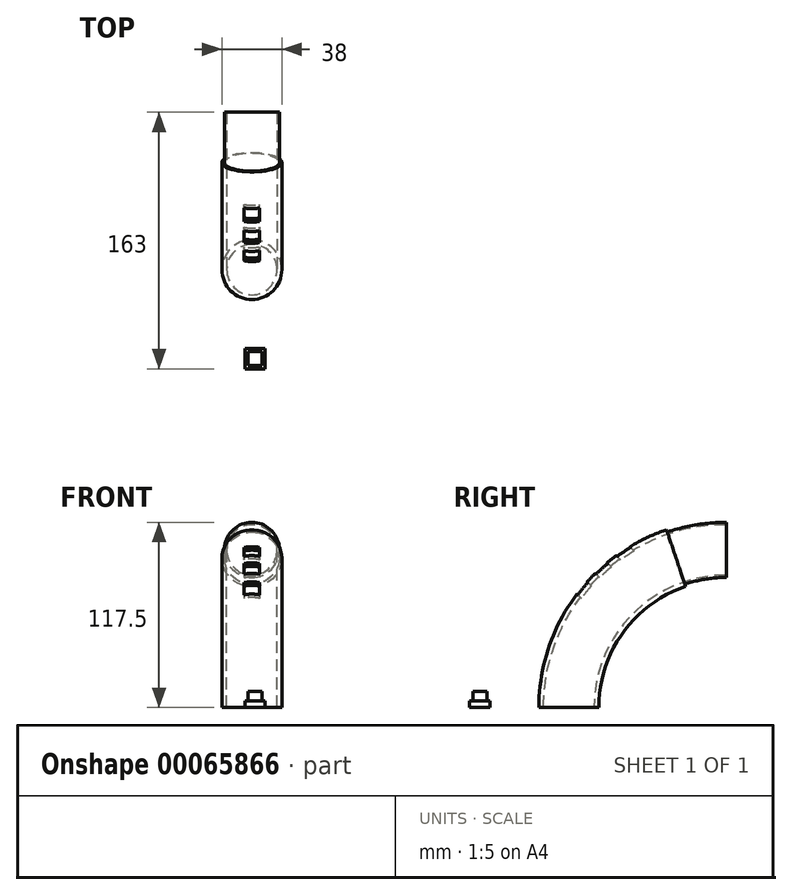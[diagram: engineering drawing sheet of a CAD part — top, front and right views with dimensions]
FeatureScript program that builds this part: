
annotation { "Feature Type Name" : "Feature", "Feature Type Description" : "" }
export const myFeature = defineFeature(function(context is Context, id is Id, definition is map)
    precondition{}
    {
        {
            var Q0;
            Q0=qCreatedBy(makeId("Front.planeOp"),FACE);
            cPlane(context, id + "F0", {"entities" : qUnion([Q0]), "cplaneType" : CPlaneType.OFFSET, "offset" : 100 * mm, "oppositeDirection" : true, "width" : 150 * mm, "height" : 150 * mm});
        }
        {
            var Q0;
            Q0=qCreatedBy(makeId("Top.planeOp"),FACE);
            var sketch = newSketch(context, id + "F1", { "sketchPlane" : qUnion([Q0])});
            skCircle(sketch, "E0", {"center": v(0, 0) * mm, "radius": 19 * mm});
            skCircle(sketch, "E1", {"center": v(0, 0) * mm, "radius": 17.5 * mm});
            skSolve(sketch);
        }
        {
            var Q0;
            Q0=qCreatedBy(makeId("Right.planeOp"),FACE);
            var sketch = newSketch(context, id + "F2", { "sketchPlane" : qUnion([Q0])});
            skLineSegment(sketch, "E2", {"start": v(0, 0) * mm, "end": v(100, 0) * mm});
            skArc(sketch, "E3", {"start": v(0, 0) * mm, "mid": v(29.29, 70.71) * mm, "end": v(100, 100) * mm});
            skSolve(sketch);
        }
        {
            var Q0;
            Q0=qCreatedBy(id+"F0.planeOp",FACE);
            var sketch = newSketch(context, id + "F3", { "sketchPlane" : qUnion([Q0])});
            skLineSegment(sketch, "E4", {"start": v(0, 0) * mm, "end": v(0, 100) * mm});
            skCircle(sketch, "E5", {"center": v(0, 100) * mm, "radius": 17.5 * mm});
            skCircle(sketch, "E6", {"center": v(0, 100) * mm, "radius": 16 * mm});
            skSolve(sketch);
        }
        {
            var Q0;
            Q0=qCreatedBy(makeId("Right.planeOp"),FACE);
            var sketch = newSketch(context, id + "F4", { "sketchPlane" : qUnion([Q0])});
            skLineSegment(sketch, "E7", {"start": v(0, 0) * mm, "end": v(100, 0) * mm});
            skArc(sketch, "E8", {"start": v(0, 0) * mm, "mid": v(18.8, 58.37) * mm, "end": v(68.15, 94.8) * mm});
            skSolve(sketch);
        }
        {
            var Q0;
            Q0=qCreatedBy(makeId("Right.planeOp"),FACE);
            var sketch = newSketch(context, id + "F5", { "sketchPlane" : qUnion([Q0])});
            skLineSegment(sketch, "E9", {"start": v(0, 0) * mm, "end": v(113.13, 113.13) * mm, "construction": true});
            skSolve(sketch);
        }
        {
            var Q0;
            Q0=makeQuery(id+"F3.imprint","IMPRINT",FACE,{"disambiguationData":[TD([[makeQuery(id+"F3.imprint","IMPRINT",EDGE,{"derivedFrom":sQuery(id+"F3.wireOp",EDGE,"E5")}),1.0]])]});
            var Q1;
            Q1=sQuery(id+"F2.wireOp",EDGE,"E3");
            sweep(context, id + "F6", {"profiles" : qUnion([Q0]), "path" : qUnion([Q1])});
        }
        {
            var Q0;
            Q0 = qSketchRegion(id + "F1", true);
            var Q1;
            Q1=sQuery(id+"F4.wireOp",EDGE,"E8");
            sweep(context, id + "F7", {"operationType" : NewBodyOperationType.ADD, "profiles" : qUnion([Q0]), "path" : qUnion([Q1])});
        }
        {
            var Q0;
            Q0 = qBodyType(qCreatedBy(id + "F5" ,EDGE), BodyType.WIRE);
            cPlane(context, id + "F8", {"entities" : qUnion([Q0]), "cplaneType" : CPlaneType.LINE_ANGLE, "offset" : 150 * mm, "angle" : 0 * degree, "width" : 150 * mm, "height" : 150 * mm});
        }
        {
            var Q0;
            Q0=qCreatedBy(id+"F8.planeOp",FACE);
            var sketch = newSketch(context, id + "F9", { "sketchPlane" : qUnion([Q0])});
            skLineSegment(sketch, "E10.rect.bottom", {"start": v(5, 89.53) * mm, "end": v(-5, 89.53) * mm});
            skPoint(sketch, "E10.rect.middle", {"position": v(0, 82.5) * mm});
            skLineSegment(sketch, "E11.top", {"start": v(-5, 99.53) * mm, "end": v(5, 99.53) * mm});
            skLineSegment(sketch, "E11.left", {"start": v(-5, 89.53) * mm, "end": v(-5, 99.53) * mm});
            skLineSegment(sketch, "E11.right", {"start": v(5, 89.53) * mm, "end": v(5, 99.53) * mm});
            skLineSegment(sketch, "E12.bottom", {"start": v(-5, 82.03) * mm, "end": v(5, 82.03) * mm});
            skLineSegment(sketch, "E12.top", {"start": v(-5, 72.03) * mm, "end": v(5, 72.03) * mm});
            skLineSegment(sketch, "E12.left", {"start": v(-5, 82.03) * mm, "end": v(-5, 72.03) * mm});
            skLineSegment(sketch, "E12.right", {"start": v(5, 82.03) * mm, "end": v(5, 72.03) * mm});
            skLineSegment(sketch, "E13.bottom", {"start": v(5, 64.53) * mm, "end": v(-5, 64.53) * mm});
            skLineSegment(sketch, "E13.top", {"start": v(5, 54.53) * mm, "end": v(-5, 54.53) * mm});
            skLineSegment(sketch, "E13.left", {"start": v(5, 64.53) * mm, "end": v(5, 54.53) * mm});
            skLineSegment(sketch, "E13.right", {"start": v(-5, 64.53) * mm, "end": v(-5, 54.53) * mm});
            skSolve(sketch);
        }
        {
            var Q0;
            Q0=makeQuery(id+"F9.imprint","IMPRINT",FACE,{"disambiguationData":[TD([[makeQuery(id+"F9.imprint","IMPRINT",EDGE,{"derivedFrom":sQuery(id+"F9.wireOp",EDGE,"E10.rect.bottom")}),-1.0]])]});
            var Q1;
            Q1=makeQuery(id+"F9.imprint","IMPRINT",FACE,{"disambiguationData":[TD([[makeQuery(id+"F9.imprint","IMPRINT",EDGE,{"derivedFrom":sQuery(id+"F9.wireOp",EDGE,"E12.bottom")}),-1.0]])]});
            var Q2;
            Q2=makeQuery(id+"F9.imprint","IMPRINT",FACE,{"disambiguationData":[TD([[makeQuery(id+"F9.imprint","IMPRINT",EDGE,{"derivedFrom":sQuery(id+"F9.wireOp",EDGE,"E13.bottom")}),1.0]])]});
            extrude(context, id + "F10", {"entities" : qUnion([Q0, Q1, Q2]), "operationType" : NewBodyOperationType.REMOVE, "depth" : 50 * mm, "hasSecondDirection" : true, "secondDirectionOppositeDirection" : false, "secondDirectionDepth" : 25 * mm});
        }
        {
            var Q0;
            Q0=qCreatedBy(makeId("Top.planeOp"),FACE);
            var sketch = newSketch(context, id + "F11", { "sketchPlane" : qUnion([Q0])});
            skLineSegment(sketch, "E14.rect.bottom", {"start": v(-4.5, -50) * mm, "end": v(8.5, -50) * mm});
            skLineSegment(sketch, "E14.rect.top", {"start": v(-4.5, -63) * mm, "end": v(8.5, -63) * mm});
            skLineSegment(sketch, "E14.rect.left", {"start": v(-4.5, -50) * mm, "end": v(-4.5, -63) * mm});
            skLineSegment(sketch, "E14.rect.right", {"start": v(8.5, -50) * mm, "end": v(8.5, -63) * mm});
            skPoint(sketch, "E14.rect.middle", {"position": v(2, -56.5) * mm});
            skLineSegment(sketch, "E15.rect.bottom", {"start": v(-2.5, -52) * mm, "end": v(6.5, -52) * mm});
            skLineSegment(sketch, "E15.rect.top", {"start": v(-2.5, -61) * mm, "end": v(6.5, -61) * mm});
            skLineSegment(sketch, "E15.rect.left", {"start": v(-2.5, -52) * mm, "end": v(-2.5, -61) * mm});
            skLineSegment(sketch, "E15.rect.right", {"start": v(6.5, -52) * mm, "end": v(6.5, -61) * mm});
            skSolve(sketch);
        }
        {
            var Q0;
            Q0=makeQuery(id+"F11.imprint","IMPRINT",FACE,{"disambiguationData":[TD([[makeQuery(id+"F11.imprint","IMPRINT",EDGE,{"derivedFrom":sQuery(id+"F11.wireOp",EDGE,"E15.rect.bottom")}),-1.0]])]});
            extrude(context, id + "F12", {"entities" : qUnion([Q0]), "depth" : 10 * mm});
        }
        {
            var Q0;
            Q0=makeQuery(id+"F11.imprint","IMPRINT",FACE,{"disambiguationData":[TD([[makeQuery(id+"F11.imprint","IMPRINT",EDGE,{"derivedFrom":sQuery(id+"F11.wireOp",EDGE,"E14.rect.bottom")}),-1.0]])]});
            extrude(context, id + "F13", {"entities" : qUnion([Q0]), "operationType" : NewBodyOperationType.ADD, "depth" : 4 * mm});
        }
    });
